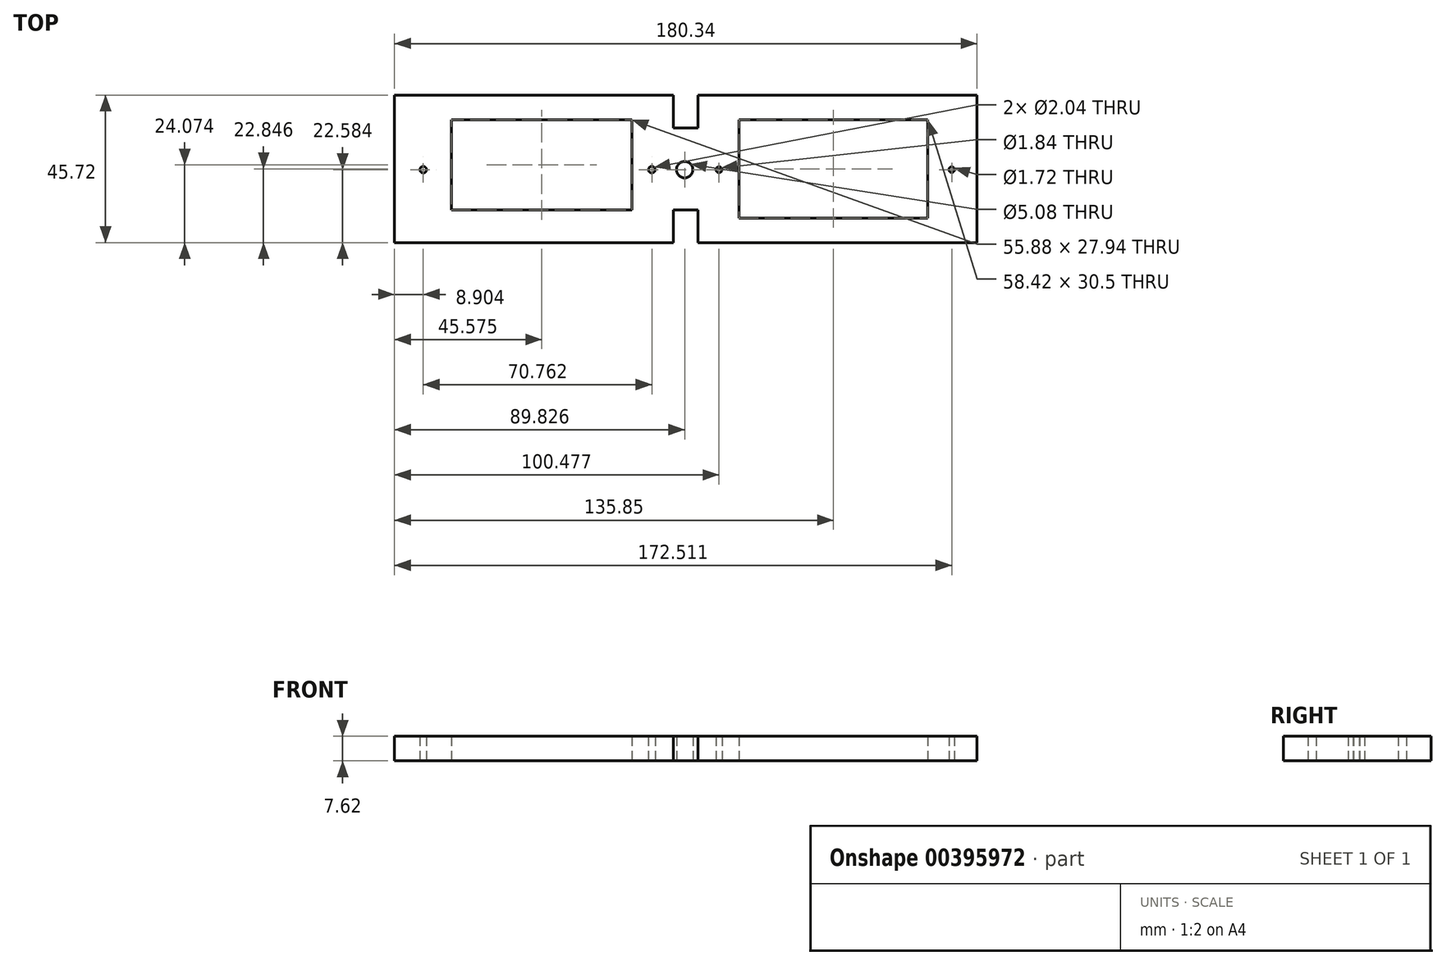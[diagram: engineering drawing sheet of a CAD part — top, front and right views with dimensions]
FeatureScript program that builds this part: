
annotation { "Feature Type Name" : "Feature", "Feature Type Description" : "" }
export const myFeature = defineFeature(function(context is Context, id is Id, definition is map)
    precondition{}
    {
        {
            var Q0;
            Q0=qCreatedBy(makeId("Top.planeOp"),FACE);
            var sketch = newSketch(context, id + "F0", { "sketchPlane" : qUnion([Q0])});
            skLineSegment(sketch, "E0.bottom", {"start": v(-162.2, 78.82) * mm, "end": v(18.13, 78.82) * mm});
            skLineSegment(sketch, "E0.top", {"start": v(-162.2, 33.1) * mm, "end": v(18.13, 33.1) * mm});
            skLineSegment(sketch, "E0.left", {"start": v(-162.2, 78.82) * mm, "end": v(-162.2, 33.1) * mm});
            skLineSegment(sketch, "E0.right", {"start": v(18.13, 78.82) * mm, "end": v(18.13, 33.1) * mm});
            skSolve(sketch);
        }
        {
            var Q0;
            Q0=makeQuery(id+"F0.imprint","IMPRINT",FACE,{"disambiguationData":[TD([[makeQuery(id+"F0.imprint","IMPRINT",EDGE,{"derivedFrom":sQuery(id+"F0.wireOp",EDGE,"E0.bottom")}),-1.0]])]});
            extrude(context, id + "F1", {"entities" : qUnion([Q0]), "depth" : 7.62 * mm});
        }
        {
            var Q0;
            Q0=qCreatedBy(makeId("Top.planeOp"),FACE);
            var sketch = newSketch(context, id + "F2", { "sketchPlane" : qUnion([Q0])});
            skLineSegment(sketch, "E1", {"start": v(-162.25, 33.1) * mm, "end": v(-75.89, 33.1) * mm});
            skLineSegment(sketch, "E2", {"start": v(-75.89, 33.1) * mm, "end": v(-68.27, 33.1) * mm});
            skLineSegment(sketch, "E3", {"start": v(-68.27, 33.1) * mm, "end": v(18.1, 33.1) * mm});
            skPoint(sketch, "E3.endSnap0", {"position": v(-119.07, 33.1) * mm});
            skLineSegment(sketch, "E4", {"start": v(-68.27, 33.1) * mm, "end": v(-68.27, 43.26) * mm});
            skLineSegment(sketch, "E5", {"start": v(-68.27, 43.26) * mm, "end": v(-75.89, 43.26) * mm});
            skLineSegment(sketch, "E6", {"start": v(-75.89, 43.26) * mm, "end": v(-75.89, 33.1) * mm});
            skLineSegment(sketch, "E7.top", {"start": v(-75.89, 43.26) * mm, "end": v(-68.27, 43.26) * mm});
            skLineSegment(sketch, "E7.left", {"start": v(-75.89, 33.1) * mm, "end": v(-75.89, 43.26) * mm});
            skSolve(sketch);
        }
        {
            var Q0;
            Q0=makeQuery(id+"F2.imprint","IMPRINT",FACE,{"disambiguationData":[TD([[makeQuery(id+"F2.imprint","IMPRINT",EDGE,{"derivedFrom":sQuery(id+"F2.wireOp",EDGE,"E2")}),1.0]])]});
            extrude(context, id + "F3", {"entities" : qUnion([Q0]), "operationType" : NewBodyOperationType.REMOVE, "oppositeDirection" : true, "depth" : -25.4 * mm});
        }
        {
            var Q0;
            Q0=qCreatedBy(makeId("Top.planeOp"),FACE);
            var sketch = newSketch(context, id + "F4", { "sketchPlane" : qUnion([Q0])});
            skLineSegment(sketch, "E8", {"start": v(-75.89, 43.26) * mm, "end": v(-75.89, 78.82) * mm});
            skLineSegment(sketch, "E9", {"start": v(-75.89, 78.82) * mm, "end": v(-68.27, 78.82) * mm});
            skLineSegment(sketch, "E10", {"start": v(-68.27, 78.82) * mm, "end": v(-68.27, 68.66) * mm});
            skLineSegment(sketch, "E11", {"start": v(-68.27, 68.66) * mm, "end": v(-75.89, 68.66) * mm});
            skLineSegment(sketch, "E12.top", {"start": v(-75.89, 68.66) * mm, "end": v(-68.27, 68.66) * mm});
            skLineSegment(sketch, "E12.left", {"start": v(-75.89, 78.82) * mm, "end": v(-75.89, 68.66) * mm});
            skSolve(sketch);
        }
        {
            var Q0;
            Q0=makeQuery(id+"F4.imprint","IMPRINT",FACE,{"disambiguationData":[TD([[makeQuery(id+"F4.imprint","IMPRINT",EDGE,{"derivedFrom":sQuery(id+"F4.wireOp",EDGE,"E9")}),-1.0]])]});
            extrude(context, id + "F5", {"entities" : qUnion([Q0]), "operationType" : NewBodyOperationType.REMOVE, "oppositeDirection" : true, "depth" : -25.4 * mm});
        }
        {
            var Q0;
            Q0=qCreatedBy(makeId("Top.planeOp"),FACE);
            var sketch = newSketch(context, id + "F6", { "sketchPlane" : qUnion([Q0])});
            skLineSegment(sketch, "E13", {"start": v(18.1, 78.77) * mm, "end": v(2.85, 78.77) * mm});
            skLineSegment(sketch, "E14", {"start": v(2.85, 78.77) * mm, "end": v(2.85, 71.2) * mm});
            skLineSegment(sketch, "E15", {"start": v(2.85, 71.2) * mm, "end": v(2.85, 43.25) * mm});
            skLineSegment(sketch, "E16", {"start": v(-68.27, 78.81) * mm, "end": v(-68.27, 78.81) * mm});
            skLineSegment(sketch, "E17", {"start": v(-68.27, 78.81) * mm, "end": v(-55.57, 78.81) * mm});
            skLineSegment(sketch, "E18", {"start": v(-55.57, 78.81) * mm, "end": v(-55.57, 78.81) * mm});
            skLineSegment(sketch, "E19", {"start": v(-55.57, 78.81) * mm, "end": v(-55.57, 71.2) * mm});
            skLineSegment(sketch, "E20", {"start": v(2.85, 33.08) * mm, "end": v(2.85, 40.7) * mm});
            skLineSegment(sketch, "E21.bottom", {"start": v(2.85, 40.7) * mm, "end": v(-55.57, 40.7) * mm});
            skLineSegment(sketch, "E21.top", {"start": v(2.85, 71.2) * mm, "end": v(-55.57, 71.2) * mm});
            skLineSegment(sketch, "E21.left", {"start": v(2.85, 40.7) * mm, "end": v(2.85, 71.2) * mm});
            skLineSegment(sketch, "E21.right", {"start": v(-55.57, 40.7) * mm, "end": v(-55.57, 71.2) * mm});
            skSolve(sketch);
        }
        {
            var Q0;
            {var subQ0=sQuery(id+"F6.wireOp",EDGE,"E21.bottom");Q0=makeQuery(id+"F6.imprint","IMPRINT",FACE,{"disambiguationData":[TD([[makeQuery(id+"F6.imprint","IMPRINT",EDGE,{"derivedFrom":subQ0}),-1.0]])]});}
            extrude(context, id + "F7", {"entities" : qUnion([Q0]), "operationType" : NewBodyOperationType.REMOVE, "oppositeDirection" : true, "depth" : -25.4 * mm});
        }
        {
            var Q0;
            Q0=qCreatedBy(makeId("Top.planeOp"),FACE);
            var sketch = newSketch(context, id + "F8", { "sketchPlane" : qUnion([Q0])});
            skLineSegment(sketch, "E22", {"start": v(-162.35, 33.04) * mm, "end": v(-144.57, 33.04) * mm});
            skLineSegment(sketch, "E23", {"start": v(-144.57, 33.04) * mm, "end": v(-144.57, 43.2) * mm});
            skLineSegment(sketch, "E24", {"start": v(-144.57, 43.2) * mm, "end": v(-88.7, 43.2) * mm});
            skLineSegment(sketch, "E25", {"start": v(-88.7, 43.2) * mm, "end": v(-88.7, 71.14) * mm});
            skLineSegment(sketch, "E26.top", {"start": v(-144.57, 71.14) * mm, "end": v(-88.7, 71.14) * mm});
            skLineSegment(sketch, "E26.left", {"start": v(-144.57, 43.2) * mm, "end": v(-144.57, 71.14) * mm});
            skSolve(sketch);
        }
        {
            var Q0;
            Q0=makeQuery(id+"F8.imprint","IMPRINT",FACE,{"disambiguationData":[TD([[makeQuery(id+"F8.imprint","IMPRINT",EDGE,{"derivedFrom":sQuery(id+"F8.wireOp",EDGE,"E24")}),1.0]])]});
            extrude(context, id + "F9", {"entities" : qUnion([Q0]), "operationType" : NewBodyOperationType.REMOVE, "oppositeDirection" : true, "depth" : -25.4 * mm});
        }
        {
            var Q0;
            Q0=qCreatedBy(makeId("Top.planeOp"),FACE);
            var sketch = newSketch(context, id + "F10", { "sketchPlane" : qUnion([Q0])});
            skLineSegment(sketch, "E27", {"start": v(-68.3, 42.98) * mm, "end": v(-68.3, 53.14) * mm});
            skLineSegment(sketch, "E28", {"start": v(-68.3, 53.14) * mm, "end": v(-68.3, 55.68) * mm});
            skLineSegment(sketch, "E29", {"start": v(-68.3, 55.68) * mm, "end": v(-76.46, 55.68) * mm});
            skCircle(sketch, "E30", {"center": v(-72.38, 55.68) * mm, "radius": 2.54 * mm});
            skLineSegment(sketch, "E31", {"start": v(-74.92, 55.68) * mm, "end": v(-82.54, 55.68) * mm});
            skCircle(sketch, "E32", {"center": v(-82.54, 55.68) * mm, "radius": 1.02 * mm});
            skCircle(sketch, "E33", {"center": v(-61.73, 55.68) * mm, "radius": 0.92 * mm});
            skCircle(sketch, "E34", {"center": v(10.3, 55.68) * mm, "radius": 0.86 * mm});
            skCircle(sketch, "E35", {"center": v(-153.3, 55.68) * mm, "radius": 1.02 * mm});
            skSolve(sketch);
        }
        {
            var Q0;
            Q0 = qSketchRegion(id + "F10", true);
            extrude(context, id + "F11", {"entities" : qUnion([Q0]), "operationType" : NewBodyOperationType.REMOVE, "oppositeDirection" : true, "depth" : -25.4 * mm});
        }
    });
